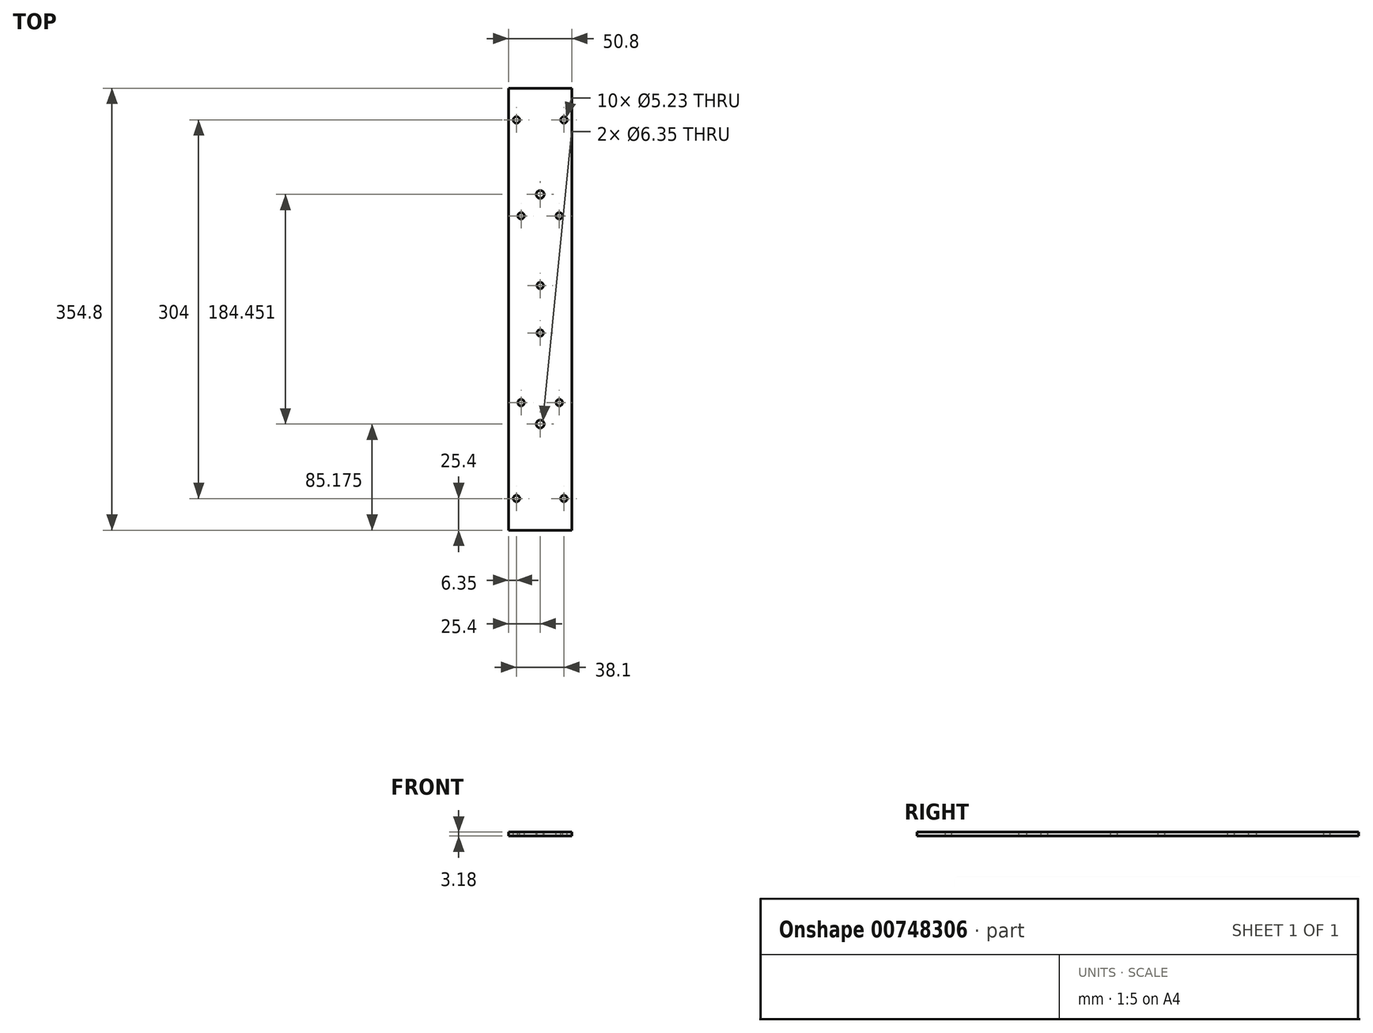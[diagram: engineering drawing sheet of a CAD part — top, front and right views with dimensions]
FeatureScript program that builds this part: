
annotation { "Feature Type Name" : "Feature", "Feature Type Description" : "" }
export const myFeature = defineFeature(function(context is Context, id is Id, definition is map)
    precondition{}
    {
        {
            var Q0;
            Q0=qCreatedBy(makeId("Front.planeOp"),FACE);
            var sketch = newSketch(context, id + "F0", { "sketchPlane" : qUnion([Q0])});
            skLineSegment(sketch, "E0.bottom", {"start": v(25.4, 1.59) * mm, "end": v(-25.4, 1.59) * mm});
            skLineSegment(sketch, "E0.top", {"start": v(25.4, -1.59) * mm, "end": v(-25.4, -1.59) * mm});
            skLineSegment(sketch, "E0.left", {"start": v(25.4, 1.59) * mm, "end": v(25.4, -1.59) * mm});
            skLineSegment(sketch, "E0.right", {"start": v(-25.4, 1.59) * mm, "end": v(-25.4, -1.59) * mm});
            skPoint(sketch, "E0.middle", {"position": v(0, 0) * mm});
            skSolve(sketch);
        }
        {
            var Q0;
            Q0=qSketchRegion(id+"F0",true);
            extrude(context, id + "F1", {"entities" : qUnion([Q0]), "depth" : 304.8 * mm + 50 * mm, "offsetDistance" : 25.4 * mm});
        }
        {
            var Q0;
            Q0=makeQuery(id+"F1.opExtrude","SWEPT_FACE",FACE,{"disambiguationData":[OSD([sQuery(id+"F0.wireOp",EDGE,"E0.bottom")])]});
            var sketch = newSketch(context, id + "F2", { "sketchPlane" : qUnion([Q0])});
            skLineSegment(sketch, "E1", {"start": v(0, -354.8) * mm, "end": v(0, 0) * mm, "construction": true});
            skLineSegment(sketch, "E2", {"start": v(-25.4, -177.4) * mm, "end": v(25.4, -177.4) * mm, "construction": true});
            skLineSegment(sketch, "E3.0", {"start": v(-25.4, -234.58) * mm, "end": v(25.4, -234.58) * mm, "construction": true});
            skLineSegment(sketch, "E4.0", {"start": v(-25.4, -120.22) * mm, "end": v(25.4, -120.22) * mm, "construction": true});
            skPoint(sketch, "E5.middle", {"position": v(0, -120.22) * mm});
            skPoint(sketch, "E6.middle", {"position": v(0, -234.58) * mm});
            skLineSegment(sketch, "E7.0", {"start": v(15.34, -507.2) * mm, "end": v(15.34, 102.4) * mm, "construction": true});
            skLineSegment(sketch, "E8.0", {"start": v(-15.34, -507.2) * mm, "end": v(-15.34, 102.4) * mm, "construction": true});
            skLineSegment(sketch, "E9.0", {"start": v(-25.4, -196.45) * mm, "end": v(25.4, -196.45) * mm, "construction": true});
            skLineSegment(sketch, "E10.0", {"start": v(-25.4, -158.35) * mm, "end": v(25.4, -158.35) * mm, "construction": true});
            skCircle(sketch, "E11", {"center": v(0, -158.35) * mm, "radius": 2.62 * mm});
            skCircle(sketch, "E12", {"center": v(0, -196.45) * mm, "radius": 2.62 * mm});
            skLineSegment(sketch, "E13", {"start": v(25.4, -25.4) * mm, "end": v(-25.4, -25.4) * mm, "construction": true});
            skLineSegment(sketch, "E14", {"start": v(25.4, -329.4) * mm, "end": v(-25.4, -329.4) * mm, "construction": true});
            skCircle(sketch, "E15", {"center": v(-19.05, -329.4) * mm, "radius": 2.62 * mm});
            skCircle(sketch, "E16", {"center": v(19.05, -329.4) * mm, "radius": 2.62 * mm});
            skCircle(sketch, "E17", {"center": v(19.05, -25.4) * mm, "radius": 2.62 * mm});
            skCircle(sketch, "E18", {"center": v(-19.05, -25.4) * mm, "radius": 2.62 * mm});
            skLineSegment(sketch, "E19.0", {"start": v(-19.05, -354.8) * mm, "end": v(-19.05, -24.6) * mm, "construction": true});
            skLineSegment(sketch, "E20.0", {"start": v(19.05, -354.8) * mm, "end": v(19.05, -24.6) * mm, "construction": true});
            skLineSegment(sketch, "E21.0", {"start": v(-25.4, -252.4) * mm, "end": v(25.4, -252.4) * mm, "construction": true});
            skCircle(sketch, "E22", {"center": v(-15.34, -252.4) * mm, "radius": 2.62 * mm});
            skCircle(sketch, "E23", {"center": v(15.34, -252.4) * mm, "radius": 2.62 * mm});
            skLineSegment(sketch, "E24.0", {"start": v(-25.4, -102.4) * mm, "end": v(25.4, -102.4) * mm, "construction": true});
            skCircle(sketch, "E25", {"center": v(15.34, -102.4) * mm, "radius": 2.62 * mm});
            skCircle(sketch, "E26", {"center": v(-15.34, -102.4) * mm, "radius": 2.62 * mm});
            skCircle(sketch, "E27", {"center": v(0, -269.63) * mm, "radius": 3.18 * mm});
            skCircle(sketch, "E28", {"center": v(0, -85.17) * mm, "radius": 3.18 * mm});
            skSolve(sketch);
        }
        {
            var Q0;
            Q0=qSketchRegion(id+"F2",true);
            extrude(context, id + "F3", {"entities" : qUnion([Q0]), "operationType" : NewBodyOperationType.REMOVE, "endBound" : BoundingType.THROUGH_ALL, "oppositeDirection" : true, "depth" : 25.4 * mm, "offsetDistance" : 25.4 * mm});
        }
    });
